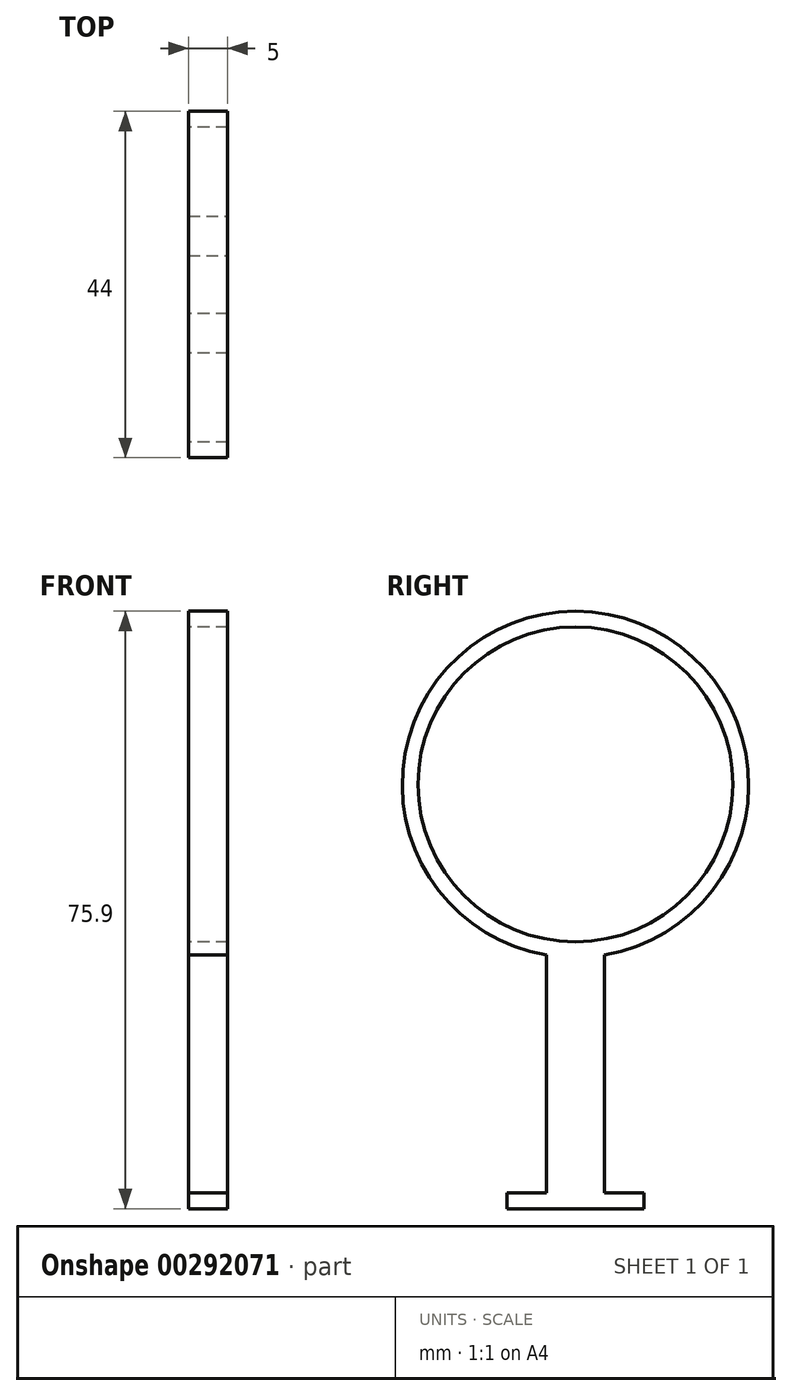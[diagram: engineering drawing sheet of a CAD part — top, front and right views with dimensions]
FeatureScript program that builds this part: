
annotation { "Feature Type Name" : "Feature", "Feature Type Description" : "" }
export const myFeature = defineFeature(function(context is Context, id is Id, definition is map)
    precondition{}
    {
        {
            var Q0;
            Q0=qCreatedBy(makeId("Right.planeOp"),FACE);
            var sketch = newSketch(context, id + "F0", { "sketchPlane" : qUnion([Q0])});
            skArc(sketch, "E0", {"start": v(3.69, 32.21) * mm, "mid": v(0, 75.9) * mm, "end": v(-3.69, 32.21) * mm});
            skCircle(sketch, "E1.0", {"center": v(0, 53.9) * mm, "radius": 20 * mm});
            skLineSegment(sketch, "E2", {"start": v(3.69, 32.21) * mm, "end": v(3.69, 0) * mm});
            skLineSegment(sketch, "E3", {"start": v(3.69, 0) * mm, "end": v(-3.69, 0) * mm});
            skLineSegment(sketch, "E4", {"start": v(-3.69, 0) * mm, "end": v(-3.69, 32.21) * mm});
            skSolve(sketch);
        }
        {
            var Q0;
            Q0=makeQuery(id+"F0.imprint","IMPRINT",FACE,{"disambiguationData":[TD([[makeQuery(id+"F0.imprint","IMPRINT",EDGE,{"derivedFrom":sQuery(id+"F0.wireOp",EDGE,"E0")}),1.0]])]});
            extrude(context, id + "F1", {"entities" : qUnion([Q0]), "depth" : 5 * mm});
        }
        {
            var Q0;
            Q0=qCreatedBy(makeId("Top.planeOp"),FACE);
            var sketch = newSketch(context, id + "F2", { "sketchPlane" : qUnion([Q0])});
            skLineSegment(sketch, "E5.0.0", {"start": v(0, -3.69) * mm, "end": v(0, 3.69) * mm});
            skLineSegment(sketch, "E5.0.1", {"start": v(0, 3.69) * mm, "end": v(5, 3.69) * mm});
            skLineSegment(sketch, "E5.0.2", {"start": v(5, 3.69) * mm, "end": v(5, -3.69) * mm});
            skLineSegment(sketch, "E5.0.3", {"start": v(5, -3.69) * mm, "end": v(0, -3.69) * mm});
            skLineSegment(sketch, "E6.0", {"start": v(0, 8.69) * mm, "end": v(5, 8.69) * mm});
            skLineSegment(sketch, "E6.1", {"start": v(0, -8.69) * mm, "end": v(0, 8.69) * mm});
            skLineSegment(sketch, "E6.2", {"start": v(5, -8.69) * mm, "end": v(0, -8.69) * mm});
            skLineSegment(sketch, "E6.3", {"start": v(5, 8.69) * mm, "end": v(5, -8.69) * mm});
            skSolve(sketch);
        }
        {
            var Q0;
            Q0 = qSketchRegion(id + "F2", true);
            extrude(context, id + "F3", {"entities" : qUnion([Q0]), "operationType" : NewBodyOperationType.ADD, "depth" : 2 * mm});
        }
    });
